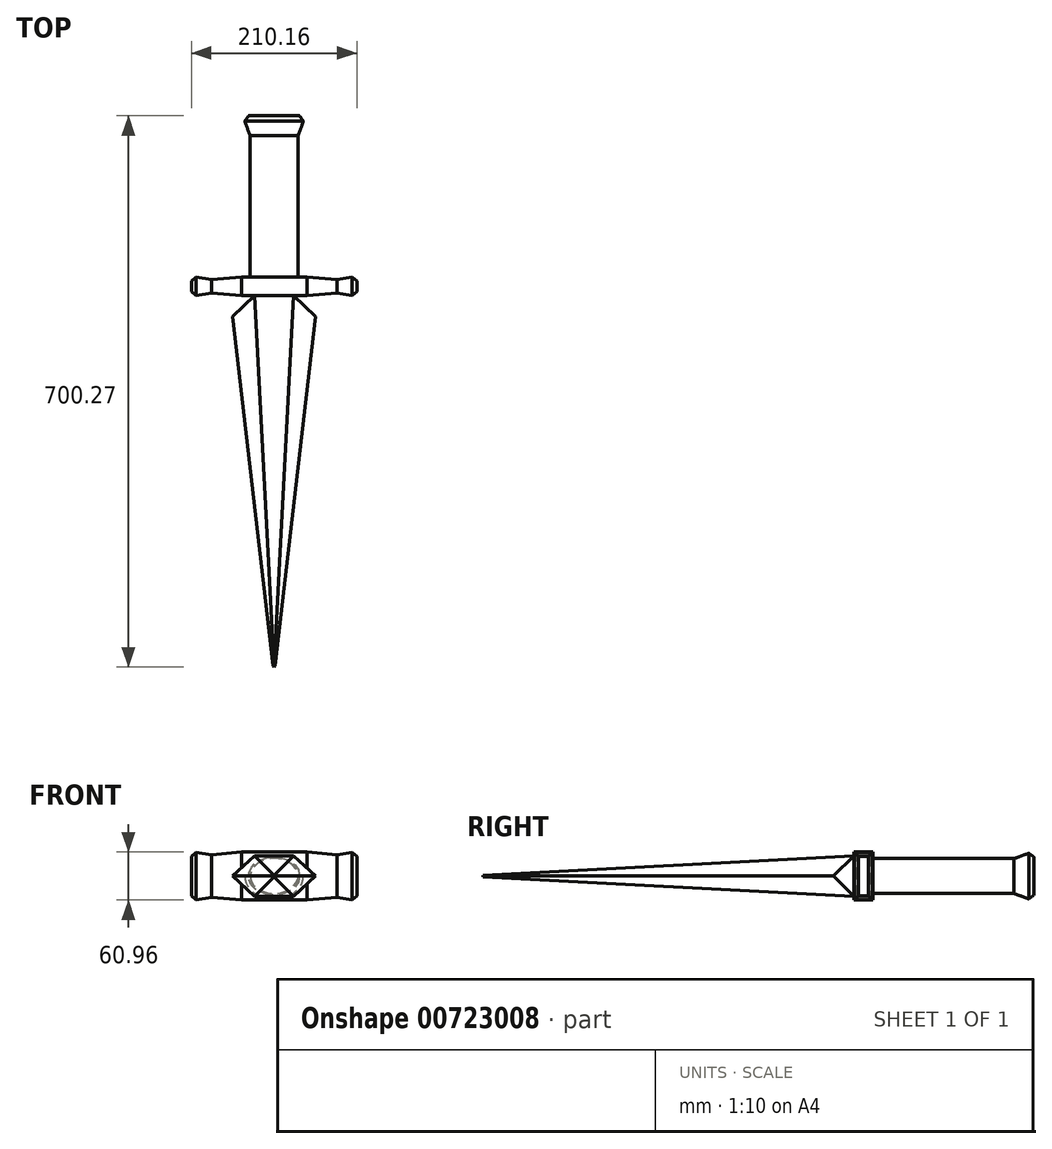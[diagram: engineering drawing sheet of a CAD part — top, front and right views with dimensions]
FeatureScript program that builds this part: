
annotation { "Feature Type Name" : "Feature", "Feature Type Description" : "" }
export const myFeature = defineFeature(function(context is Context, id is Id, definition is map)
    precondition{}
    {
        {
            var Q0;
            Q0=qCreatedBy(makeId("Front.planeOp"),FACE);
            var sketch = newSketch(context, id + "F0", { "sketchPlane" : qUnion([Q0])});
            skLineSegment(sketch, "E0.bottom", {"start": v(24.72, -25.87) * mm, "end": v(-24.72, -25.87) * mm});
            skLineSegment(sketch, "E0.top", {"start": v(24.72, 25.87) * mm, "end": v(-24.72, 25.87) * mm});
            skLineSegment(sketch, "E0.left", {"start": v(24.72, -25.87) * mm, "end": v(24.72, 25.87) * mm});
            skLineSegment(sketch, "E0.right", {"start": v(-24.72, -25.87) * mm, "end": v(-24.72, 25.87) * mm});
            skPoint(sketch, "E0.middle", {"position": v(0, 0) * mm});
            skSolve(sketch);
        }
        {
            var Q0;
            Q0=makeQuery(id+"F0.imprint","IMPRINT",FACE,{"disambiguationData":[TD([[makeQuery(id+"F0.imprint","IMPRINT",EDGE,{"derivedFrom":sQuery(id+"F0.wireOp",EDGE,"E0.bottom")}),-1.0]])]});
            var Q1;
            Q1 = qSketchRegion(id + "F0", true);
            extrude(context, id + "F1", {"entities" : qUnion([Q0, Q1]), "depth" : 482.6 * mm, "offsetDistance" : 25.4 * mm, "hasDraft" : true, "draftAngle" : 3 * degree, "draftPullDirection" : true});
        }
        {
            var Q0;
            Q0=qCreatedBy(makeId("Top.planeOp"),FACE);
            var sketch = newSketch(context, id + "F2", { "sketchPlane" : qUnion([Q0])});
            skLineSegment(sketch, "E1.bottom", {"start": v(41.58, 0) * mm, "end": v(-41.58, 0) * mm});
            skLineSegment(sketch, "E1.top", {"start": v(41.58, 23.78) * mm, "end": v(-41.58, 23.78) * mm});
            skLineSegment(sketch, "E1.left", {"start": v(41.58, 0) * mm, "end": v(41.58, 23.78) * mm});
            skLineSegment(sketch, "E1.right", {"start": v(-41.58, 0) * mm, "end": v(-41.58, 23.78) * mm});
            skPoint(sketch, "E1.middle", {"position": v(0, 11.89) * mm});
            skSolve(sketch);
        }
        {
            var Q0;
            Q0=makeQuery(id+"F2.imprint","IMPRINT",FACE,{"disambiguationData":[TD([[makeQuery(id+"F2.imprint","IMPRINT",EDGE,{"derivedFrom":sQuery(id+"F2.wireOp",EDGE,"E1.bottom")}),-1.0]])]});
            extrude(context, id + "F3", {"entities" : qUnion([Q0]), "operationType" : NewBodyOperationType.ADD, "depth" : 30.48 * mm, "offsetDistance" : 25.4 * mm});
        }
        {
            var Q0;
            Q0=makeQuery(id+"F3.opExtrude","CAP_FACE",FACE,{"disambiguationData":[OSD([sQuery(id+"F2.wireOp",EDGE,"E1.bottom"),sQuery(id+"F2.wireOp",EDGE,"E1.top"),sQuery(id+"F2.wireOp",EDGE,"E1.left"),sQuery(id+"F2.wireOp",EDGE,"E1.right")])],"isStart":true});
            extrude(context, id + "F4", {"entities" : qUnion([Q0]), "operationType" : NewBodyOperationType.ADD, "depth" : 30.48 * mm, "offsetDistance" : 25.4 * mm});
        }
        {
            var Q0;
            {var subQ0=sQuery(id+"F2.wireOp",EDGE,"E1.left");Q0=makeQuery(id+"F4.boolean.opBoolean","MERGE",FACE,{"derivedFrom":[makeQuery(id+"F3.opExtrude","SWEPT_FACE",FACE,{"disambiguationData":[OSD([subQ0])]}),makeQuery(id+"F4.opExtrude","SWEPT_FACE",FACE,{"disambiguationData":[OSD([subQ0])]})]});}
            extrude(context, id + "F5", {"entities" : qUnion([Q0]), "operationType" : NewBodyOperationType.ADD, "depth" : 38.1 * mm, "offsetDistance" : 25.4 * mm, "hasDraft" : true, "draftAngle" : 5 * degree, "draftPullDirection" : true});
        }
        {
            var Q0;
            {var subQ0=sQuery(id+"F2.wireOp",EDGE,"E1.right");Q0=makeQuery(id+"F4.boolean.opBoolean","MERGE",FACE,{"derivedFrom":[makeQuery(id+"F3.opExtrude","SWEPT_FACE",FACE,{"disambiguationData":[OSD([subQ0])]}),makeQuery(id+"F4.opExtrude","SWEPT_FACE",FACE,{"disambiguationData":[OSD([subQ0])]})]});}
            extrude(context, id + "F6", {"entities" : qUnion([Q0]), "operationType" : NewBodyOperationType.ADD, "depth" : 38.1 * mm, "offsetDistance" : 25.4 * mm, "hasDraft" : true, "draftAngle" : 5 * degree, "draftPullDirection" : true});
        }
        {
            var Q0;
            Q0=makeQuery(id+"F6.opExtrude","CAP_FACE",FACE,{"disambiguationData":[OSD([sQuery(id+"F2.wireOp",EDGE,"E1.right")])],"isStart":false});
            extrude(context, id + "F7", {"entities" : qUnion([Q0]), "operationType" : NewBodyOperationType.ADD, "depth" : 25.4 * mm, "offsetDistance" : 25.4 * mm, "hasDraft" : true, "draftAngle" : 9 * degree});
        }
        {
            var Q0;
            Q0=makeQuery(id+"F5.opExtrude","CAP_FACE",FACE,{"disambiguationData":[OSD([sQuery(id+"F2.wireOp",EDGE,"E1.left")])],"isStart":false});
            extrude(context, id + "F8", {"entities" : qUnion([Q0]), "operationType" : NewBodyOperationType.ADD, "depth" : 25.4 * mm, "offsetDistance" : 25.4 * mm, "hasDraft" : true, "draftAngle" : 9 * degree});
        }
        {
            var Q0;
            Q0=makeQuery(id+"F1.opExtrude","SWEPT_FACE",FACE,{"disambiguationData":[OSD([sQuery(id+"F0.wireOp",EDGE,"E0.left")])]});
            extrude(context, id + "F9", {"entities" : qUnion([Q0]), "operationType" : NewBodyOperationType.ADD, "depth" : 30.48 * mm, "offsetDistance" : 25.4 * mm, "hasDraft" : true, "draftAngle" : 40 * degree, "draftPullDirection" : true});
        }
        {
            var Q0;
            Q0=makeQuery(id+"F1.opExtrude","SWEPT_FACE",FACE,{"disambiguationData":[OSD([sQuery(id+"F0.wireOp",EDGE,"E0.right")])]});
            extrude(context, id + "F10", {"entities" : qUnion([Q0]), "operationType" : NewBodyOperationType.ADD, "depth" : 30.48 * mm, "offsetDistance" : 25.4 * mm, "hasDraft" : true, "draftAngle" : 40 * degree, "draftPullDirection" : true});
        }
        {
            var Q0;
            Q0=qCreatedBy(makeId("Front.planeOp"),FACE);
            var sketch = newSketch(context, id + "F11", { "sketchPlane" : qUnion([Q0])});
            skEllipse(sketch, "E2", {"center": v(0, 0) * mm, "majorRadius": 22.23 * mm, "minorRadius": 30.48 * mm, "majorAxis": v(0, 1)});
            skSolve(sketch);
        }
        {
            var Q0;
            Q0 = qSketchRegion(id + "F11", true);
            extrude(context, id + "F12", {"entities" : qUnion([Q0]), "operationType" : NewBodyOperationType.ADD, "oppositeDirection" : true, "depth" : 203.2 * mm, "offsetDistance" : 25.4 * mm});
        }
        {
            var Q0;
            Q0=makeQuery(id+"F12.opExtrude","CAP_FACE",FACE,{"disambiguationData":[OSD([sQuery(id+"F11.wireOp",EDGE,"E2")])],"isStart":false});
            extrude(context, id + "F13", {"entities" : qUnion([Q0]), "operationType" : NewBodyOperationType.ADD, "depth" : 25.4 * mm, "offsetDistance" : 25.4 * mm, "hasDraft" : true, "draftAngle" : 20 * degree});
        }
        {
            var Q0;
            Q0=makeQuery(id+"F7.opExtrude","CAP_EDGE",EDGE,{"disambiguationData":[OSD([sQuery(id+"F2.wireOp",EDGE,"E1.top"),sQuery(id+"F2.wireOp",EDGE,"E1.right")])],"isStart":false});
            var Q1;
            {var subQ0=sQuery(id+"F2.wireOp",EDGE,"E1.right");Q1=makeQuery(id+"F7.opExtrude","CAP_EDGE",EDGE,{"disambiguationData":[OSD([subQ0]),TDD([makeQuery(id+"F6.opExtrude","CAP_EDGE",EDGE,{"disambiguationData":[OSD([subQ0]),TDD([makeQuery(id+"F3.opExtrude","CAP_EDGE",EDGE,{"disambiguationData":[OSD([subQ0])],"isStart":false})])],"isStart":false})])],"isStart":false});}
            var Q2;
            Q2=makeQuery(id+"F7.opExtrude","CAP_EDGE",EDGE,{"disambiguationData":[OSD([sQuery(id+"F2.wireOp",EDGE,"E1.bottom"),sQuery(id+"F2.wireOp",EDGE,"E1.right")])],"isStart":false});
            var Q3;
            {var subQ0=sQuery(id+"F2.wireOp",EDGE,"E1.right");Q3=makeQuery(id+"F7.opExtrude","CAP_EDGE",EDGE,{"disambiguationData":[OSD([subQ0]),TDD([makeQuery(id+"F6.opExtrude","CAP_EDGE",EDGE,{"disambiguationData":[OSD([subQ0]),TDD([makeQuery(id+"F4.opExtrude","CAP_EDGE",EDGE,{"disambiguationData":[OSD([subQ0])],"isStart":false})])],"isStart":false})])],"isStart":false});}
            var Q4;
            Q4=makeQuery(id+"F8.opExtrude","CAP_EDGE",EDGE,{"disambiguationData":[OSD([sQuery(id+"F2.wireOp",EDGE,"E1.bottom"),sQuery(id+"F2.wireOp",EDGE,"E1.left")])],"isStart":false});
            var Q5;
            {var subQ0=sQuery(id+"F2.wireOp",EDGE,"E1.left");Q5=makeQuery(id+"F8.opExtrude","CAP_EDGE",EDGE,{"disambiguationData":[OSD([subQ0]),TDD([makeQuery(id+"F5.opExtrude","CAP_EDGE",EDGE,{"disambiguationData":[OSD([subQ0]),TDD([makeQuery(id+"F3.opExtrude","CAP_EDGE",EDGE,{"disambiguationData":[OSD([subQ0])],"isStart":false})])],"isStart":false})])],"isStart":false});}
            var Q6;
            Q6=makeQuery(id+"F8.opExtrude","CAP_EDGE",EDGE,{"disambiguationData":[OSD([sQuery(id+"F2.wireOp",EDGE,"E1.top"),sQuery(id+"F2.wireOp",EDGE,"E1.left")])],"isStart":false});
            var Q7;
            {var subQ0=sQuery(id+"F2.wireOp",EDGE,"E1.left");Q7=makeQuery(id+"F8.opExtrude","CAP_EDGE",EDGE,{"disambiguationData":[OSD([subQ0]),TDD([makeQuery(id+"F5.opExtrude","CAP_EDGE",EDGE,{"disambiguationData":[OSD([subQ0]),TDD([makeQuery(id+"F4.opExtrude","CAP_EDGE",EDGE,{"disambiguationData":[OSD([subQ0])],"isStart":false})])],"isStart":false})])],"isStart":false});}
            chamfer(context, id + "F14", {"entities" : qUnion([Q0, Q1, Q2, Q3, Q4, Q5, Q6, Q7]), "width" : 5.08 * mm, "tangentPropagation" : true});
        }
        {
            var Q0;
            Q0=makeQuery(id+"F13.opExtrude","CAP_EDGE",EDGE,{"disambiguationData":[OSD([sQuery(id+"F11.wireOp",EDGE,"E2")])],"isStart":false});
            chamfer(context, id + "F15", {"entities" : qUnion([Q0]), "width" : 5.08 * mm, "tangentPropagation" : true});
        }
    });
